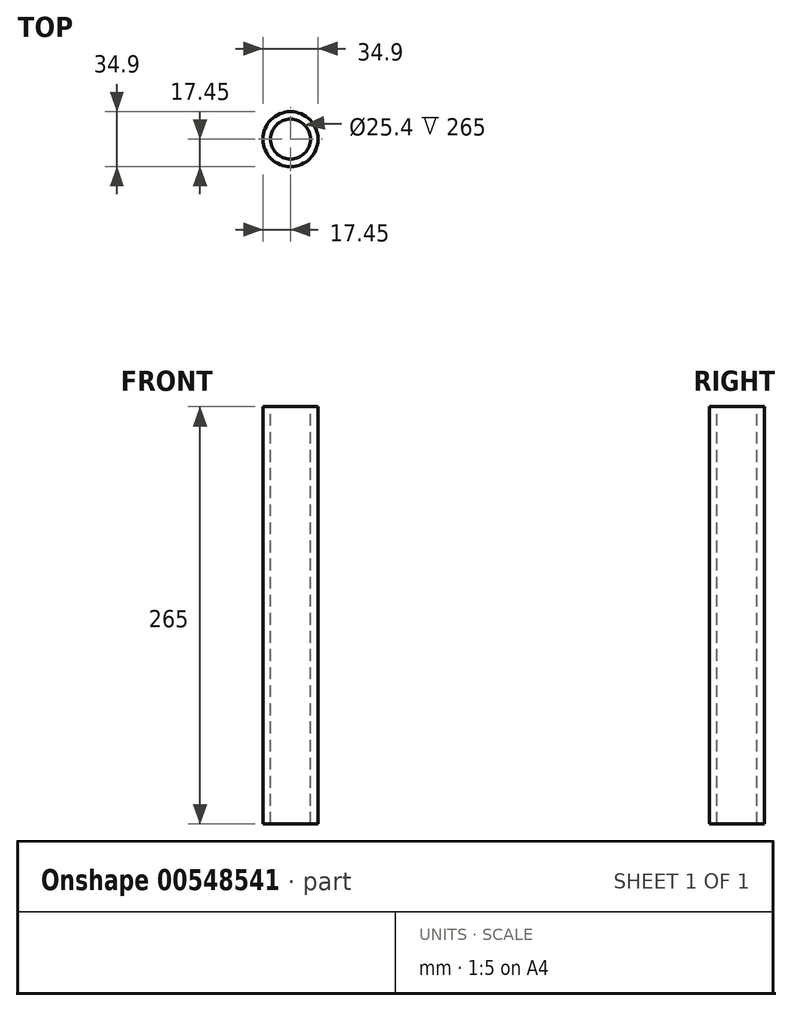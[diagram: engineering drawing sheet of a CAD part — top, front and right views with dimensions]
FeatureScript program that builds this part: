
annotation { "Feature Type Name" : "Feature", "Feature Type Description" : "" }
export const myFeature = defineFeature(function(context is Context, id is Id, definition is map)
    precondition{}
    {
        {
            var Q0;
            Q0=qCreatedBy(makeId("Top.planeOp"),FACE);
            var sketch = newSketch(context, id + "F0", { "sketchPlane" : qUnion([Q0])});
            skCircle(sketch, "E0", {"center": v(0, 0) * mm, "radius": 17.45 * mm});
            skCircle(sketch, "E1", {"center": v(0, 0) * mm, "radius": 12.7 * mm});
            skSolve(sketch);
        }
        {
            var Q0;
            Q0=makeQuery(id+"F0.imprint","IMPRINT",FACE,{"disambiguationData":[TD([[makeQuery(id+"F0.imprint","IMPRINT",EDGE,{"derivedFrom":sQuery(id+"F0.wireOp",EDGE,"E0")}),1.0]])]});
            extrude(context, id + "F1", {"entities" : qUnion([Q0]), "oppositeDirection" : true, "depth" : 265 * mm, "offsetDistance" : 25.4 * mm});
        }
    });
